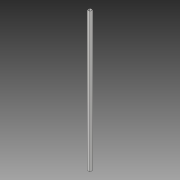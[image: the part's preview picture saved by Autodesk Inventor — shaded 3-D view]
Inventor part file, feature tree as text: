
AUTODESK INVENTOR PART (.ipt)
format: ipt  version: 2018 (Build 220112000, 112)  size: 77,824 bytes
history: native  units: in
note: dims shown in document units (in); Inventor stores cm internally (conversion verified against a paired STEP export)
features: extrude x1, sketch x1
ambient origin geometry x8: Origin, YZ Plane, XZ Plane, XY Plane, X Axis, Y Axis, Z Axis, Center Point
bodies: Solid1 (feature_tree)
feature tree (2):
  extrude  "Extrusion1"  Depth=1.0in
  sketch  "Sketch1"  dims[d0=1.0in d1=1.0in d2=0.0625in d3=48.0in d4=0.0in]
